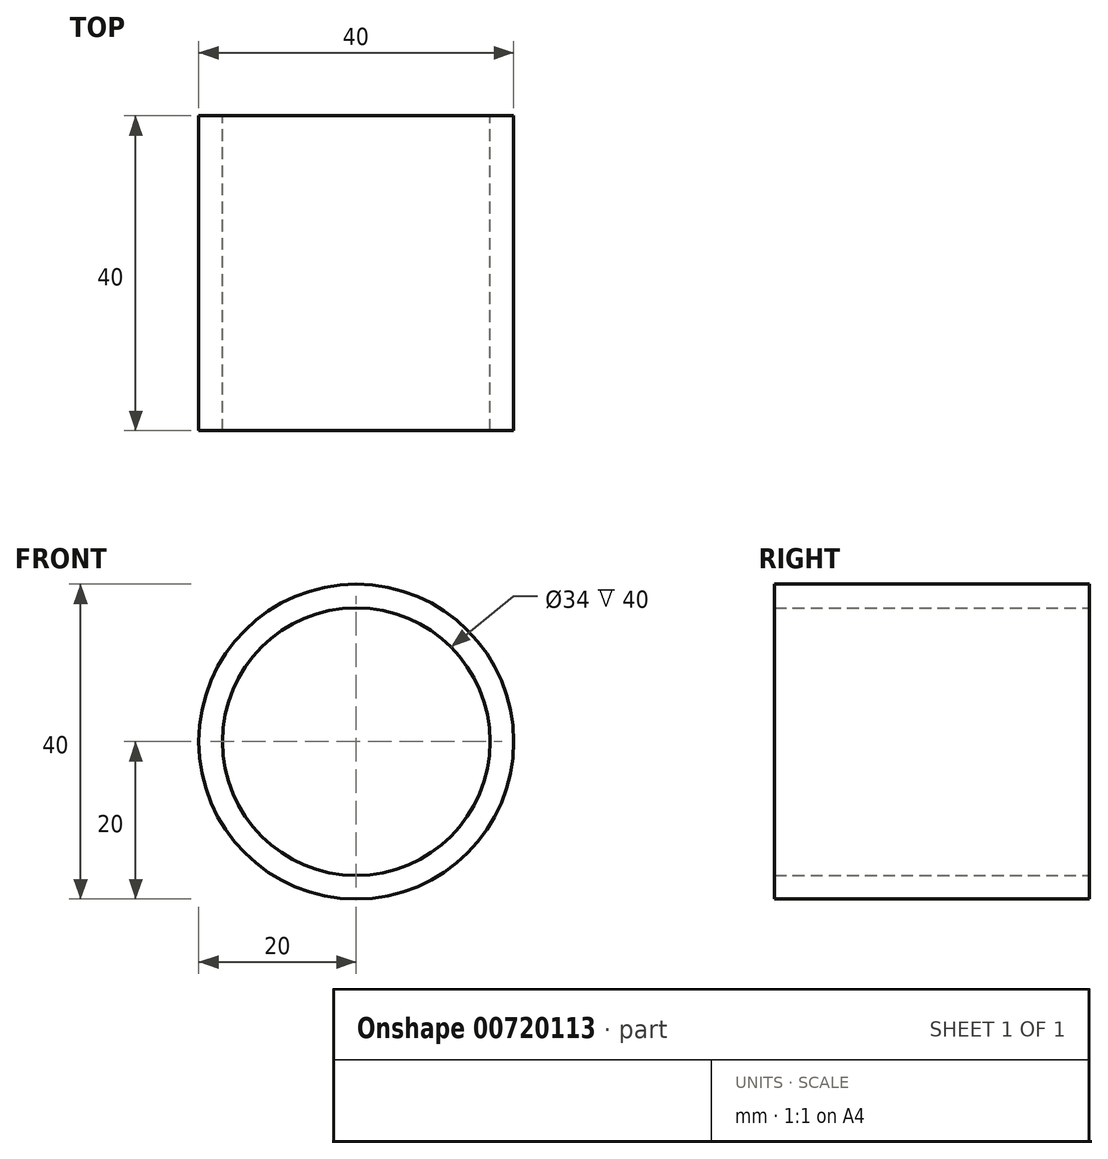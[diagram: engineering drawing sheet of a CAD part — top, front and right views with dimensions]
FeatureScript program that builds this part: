
annotation { "Feature Type Name" : "Feature", "Feature Type Description" : "" }
export const myFeature = defineFeature(function(context is Context, id is Id, definition is map)
    precondition{}
    {
        {
            var Q0;
            Q0=qCreatedBy(makeId("Front.planeOp"),FACE);
            var sketch = newSketch(context, id + "F0", { "sketchPlane" : qUnion([Q0])});
            skCircle(sketch, "E0", {"center": v(0, 0) * mm, "radius": 17 * mm});
            skCircle(sketch, "E1", {"center": v(0, 0) * mm, "radius": 20 * mm});
            skSolve(sketch);
        }
        {
            var Q0;
            Q0=makeQuery(id+"F0.imprint","IMPRINT",FACE,{"disambiguationData":[TD([[makeQuery(id+"F0.imprint","IMPRINT",EDGE,{"derivedFrom":sQuery(id+"F0.wireOp",EDGE,"E0")}),-1.0]])]});
            extrude(context, id + "F1", {"entities" : qUnion([Q0]), "depth" : 40 * mm, "offsetDistance" : 25 * mm});
        }
    });
